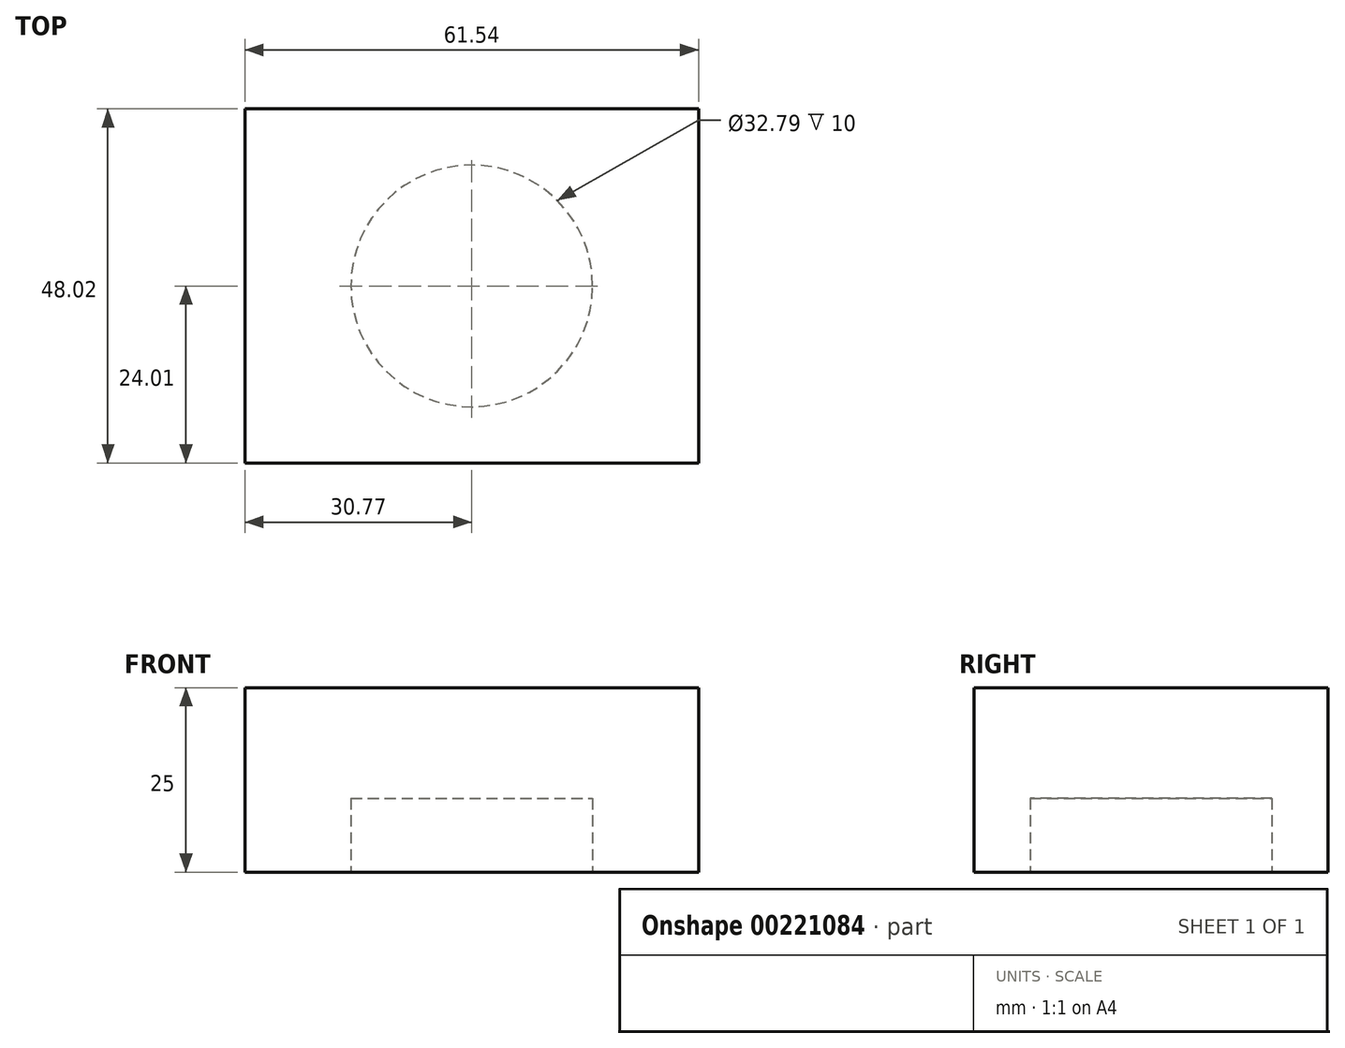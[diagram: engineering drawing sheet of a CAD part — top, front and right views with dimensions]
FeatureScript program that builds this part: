
annotation { "Feature Type Name" : "Feature", "Feature Type Description" : "" }
export const myFeature = defineFeature(function(context is Context, id is Id, definition is map)
    precondition{}
    {
        {
            var Q0;
            Q0=qCreatedBy(makeId("Top.planeOp"),FACE);
            var sketch = newSketch(context, id + "F0", { "sketchPlane" : qUnion([Q0])});
            skLineSegment(sketch, "E0.bottom", {"start": v(30.77, -24) * mm, "end": v(-30.77, -24) * mm});
            skLineSegment(sketch, "E0.top", {"start": v(30.77, 24) * mm, "end": v(-30.77, 24) * mm});
            skLineSegment(sketch, "E0.left", {"start": v(30.77, -24) * mm, "end": v(30.77, 24) * mm});
            skLineSegment(sketch, "E0.right", {"start": v(-30.77, -24) * mm, "end": v(-30.77, 24) * mm});
            skPoint(sketch, "E0.middle", {"position": v(0, 0) * mm});
            skSolve(sketch);
        }
        {
            var Q0;
            Q0 = qSketchRegion(id + "F0", true);
            extrude(context, id + "F1", {"entities" : qUnion([Q0]), "depth" : 25 * mm});
        }
        {
            var Q0;
            Q0=makeQuery(id+"F1.opExtrude","CAP_FACE",FACE,{"disambiguationData":[OSD([sQuery(id+"F0.wireOp",EDGE,"E0.bottom"),sQuery(id+"F0.wireOp",EDGE,"E0.top"),sQuery(id+"F0.wireOp",EDGE,"E0.left"),sQuery(id+"F0.wireOp",EDGE,"E0.right")])],"isStart":true});
            var sketch = newSketch(context, id + "F2", { "sketchPlane" : qUnion([Q0])});
            skCircle(sketch, "E1", {"center": v(0, 0) * mm, "radius": 16.4 * mm});
            skSolve(sketch);
        }
        {
            var Q0;
            Q0 = qSketchRegion(id + "F2", true);
            extrude(context, id + "F3", {"entities" : qUnion([Q0]), "operationType" : NewBodyOperationType.REMOVE, "oppositeDirection" : true, "depth" : 10 * mm});
        }
    });
